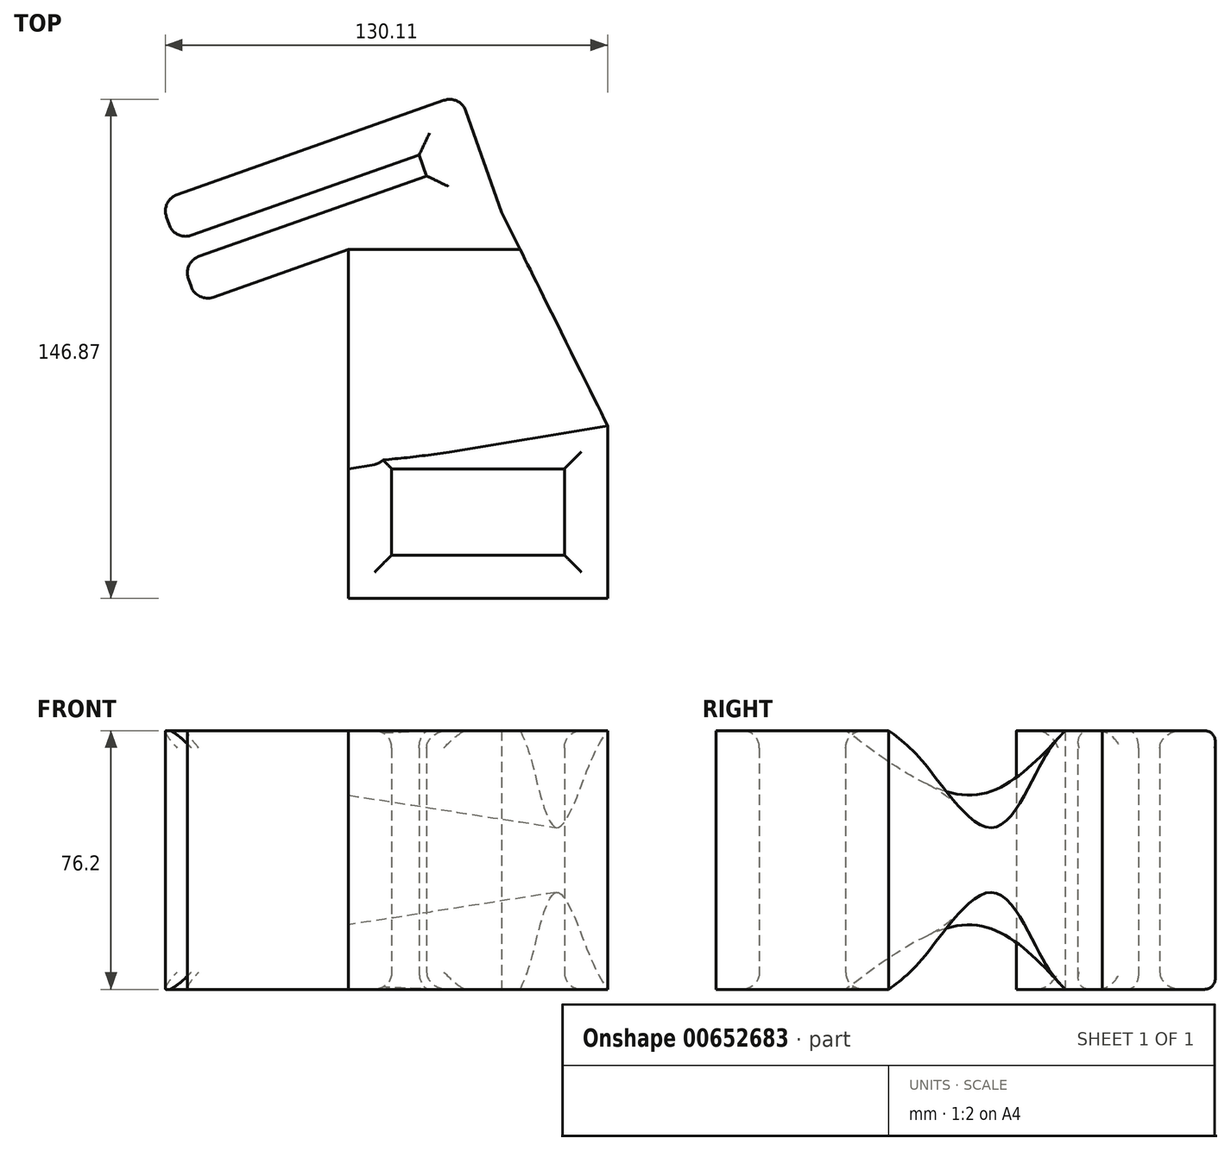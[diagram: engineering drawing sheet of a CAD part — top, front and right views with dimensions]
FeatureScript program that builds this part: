
annotation { "Feature Type Name" : "Feature", "Feature Type Description" : "" }
export const myFeature = defineFeature(function(context is Context, id is Id, definition is map)
    precondition{}
    {
        {
            var Q0;
            Q0=qCreatedBy(makeId("Top.planeOp"),FACE);
            var sketch = newSketch(context, id + "F0", { "sketchPlane" : qUnion([Q0])});
            skLineSegment(sketch, "E0.bottom", {"start": v(-25.4, -12.7) * mm, "end": v(25.4, -12.7) * mm});
            skLineSegment(sketch, "E0.top", {"start": v(-25.4, 12.7) * mm, "end": v(25.4, 12.7) * mm});
            skLineSegment(sketch, "E0.left", {"start": v(-25.4, -12.7) * mm, "end": v(-25.4, 12.7) * mm});
            skLineSegment(sketch, "E0.right", {"start": v(25.4, -12.7) * mm, "end": v(25.4, 12.7) * mm});
            skPoint(sketch, "E0.middle", {"position": v(0, 0) * mm});
            skLineSegment(sketch, "E1.bottom", {"start": v(-38.1, -25.4) * mm, "end": v(38.1, -25.4) * mm});
            skLineSegment(sketch, "E1.top", {"start": v(-38.1, 25.4) * mm, "end": v(38.1, 25.4) * mm});
            skLineSegment(sketch, "E1.left", {"start": v(-38.1, -25.4) * mm, "end": v(-38.1, 25.4) * mm});
            skLineSegment(sketch, "E1.right", {"start": v(38.1, -25.4) * mm, "end": v(38.1, 25.4) * mm});
            skLineSegment(sketch, "E2", {"start": v(0, 0) * mm, "end": v(-304.8, 0) * mm, "construction": true});
            skLineSegment(sketch, "E3", {"start": v(-304.8, 0) * mm, "end": v(-17.43, 101.6) * mm, "construction": true});
            skLineSegment(sketch, "E4", {"start": v(-89.18, 79.74) * mm, "end": v(-17.34, 105.14) * mm});
            skLineSegment(sketch, "E5", {"start": v(-17.34, 105.14) * mm, "end": v(-15.13, 98.91) * mm});
            skLineSegment(sketch, "E6", {"start": v(-15.13, 98.91) * mm, "end": v(-86.98, 73.51) * mm});
            skLineSegment(sketch, "E7", {"start": v(-89.18, 79.74) * mm, "end": v(-93.41, 91.71) * mm});
            skLineSegment(sketch, "E8", {"start": v(-93.41, 91.71) * mm, "end": v(-5.26, 122.87) * mm});
            skLineSegment(sketch, "E9", {"start": v(-5.26, 122.87) * mm, "end": v(6.98, 88.25) * mm});
            skLineSegment(sketch, "E10", {"start": v(6.98, 88.25) * mm, "end": v(38.1, 25.4) * mm});
            skLineSegment(sketch, "E11", {"start": v(-86.98, 73.51) * mm, "end": v(-82.74, 61.54) * mm});
            skLineSegment(sketch, "E12", {"start": v(-82.74, 61.54) * mm, "end": v(-38.1, 77.32) * mm});
            skLineSegment(sketch, "E13", {"start": v(-38.1, 77.32) * mm, "end": v(-38.1, 25.4) * mm});
            skSolve(sketch);
        }
        {
            var Q0;
            Q0=makeQuery(id+"F0.imprint","IMPRINT",FACE,{"disambiguationData":[TD([[makeQuery(id+"F0.imprint","IMPRINT",EDGE,{"derivedFrom":sQuery(id+"F0.wireOp",EDGE,"E1.top")}),1.0]])]});
            var Q1;
            Q1=makeQuery(id+"F0.imprint","IMPRINT",FACE,{"disambiguationData":[TD([[makeQuery(id+"F0.imprint","IMPRINT",EDGE,{"derivedFrom":sQuery(id+"F0.wireOp",EDGE,"E0.bottom")}),-1.0]])]});
            extrude(context, id + "F1", {"entities" : qUnion([Q0, Q1]), "depth" : 76.2 * mm, "offsetDistance" : 25.4 * mm});
        }
        {
            var Q0;
            Q0=makeQuery(id+"F1.opExtrude","SWEPT_FACE",FACE,{"disambiguationData":[OSD([sQuery(id+"F0.wireOp",EDGE,"E1.left"),sQuery(id+"F0.wireOp",EDGE,"E13")])]});
            var sketch = newSketch(context, id + "F2", { "sketchPlane" : qUnion([Q0])});
            skLineSegment(sketch, "E14.0", {"start": v(-12.7, 76.2) * mm, "end": v(-12.7, 0) * mm, "construction": true});
            skLineSegment(sketch, "E15.0", {"start": v(-77.32, 76.2) * mm, "end": v(-77.32, 0) * mm, "construction": true});
            skLineSegment(sketch, "E16", {"start": v(25.4, 38.1) * mm, "end": v(-77.32, 38.1) * mm});
            skFitSpline(sketch, "E17", {"points": [v(-77.32, 76.2) * mm, v(-50.46, 57.23) * mm, v(-12.7, 76.2) * mm], "startDerivative": vector(54.08, -58.32) * mm, "endDerivative": vector(74.73, 55.94) * mm});
            skFitSpline(sketch, "E18.MirrorCS", {"points": [v(-77.32, 0) * mm, v(-50.46, 18.97) * mm, v(-12.7, 0) * mm], "startDerivative": vector(54.08, 58.32) * mm, "endDerivative": vector(74.73, -55.94) * mm});
            skSolve(sketch);
        }
        {
            var Q0;
            Q0=makeQuery(id+"F1.opExtrude","SWEPT_FACE",FACE,{"disambiguationData":[OSD([sQuery(id+"F0.wireOp",EDGE,"E10")])]});
            var sketch = newSketch(context, id + "F3", { "sketchPlane" : qUnion([Q0])});
            skFitSpline(sketch, "E19.0", {"points": [v(63.76, 76.2) * mm, v(56.2, 67.09) * mm, v(40.04, 47.65) * mm, v(17.72, 66.3) * mm, v(5.86, 76.2) * mm]});
            skFitSpline(sketch, "E20.0", {"points": [v(63.76, 0) * mm, v(56.2, 9.11) * mm, v(40.04, 28.55) * mm, v(17.72, 9.9) * mm, v(5.86, 0) * mm]});
            skSolve(sketch);
        }
        {
            var Q1;
            {var subQ0=sQuery(id+"F2.wireOp",EDGE,"E17");Q1=makeQuery(id+"F2.imprint","IMPRINT",FACE,{"disambiguationData":[TD([[makeQuery(id+"F2.imprint","IMPRINT",EDGE,{"derivedFrom":subQ0}),1.0]])]});}
            var Q2;
            {var subQ0=sQuery(id+"F3.wireOp",EDGE,"E19.0");Q2=makeQuery(id+"F3.imprint","IMPRINT",FACE,{"disambiguationData":[TD([[makeQuery(id+"F3.imprint","IMPRINT",EDGE,{"derivedFrom":subQ0}),-1.0]])]});}
            loft(context, id + "F4", {"operationType" : NewBodyOperationType.REMOVE, "sheetProfilesArray" : [{ "sheetProfileEntities" : qUnion([Q1]) }, { "sheetProfileEntities" : qUnion([Q2]) }]});
        }
        {
            var Q1;
            {var subQ0=sQuery(id+"F2.wireOp",EDGE,"E18.MirrorCS");Q1=makeQuery(id+"F2.imprint","IMPRINT",FACE,{"disambiguationData":[TD([[makeQuery(id+"F2.imprint","IMPRINT",EDGE,{"derivedFrom":subQ0}),-1.0]])]});}
            var Q2;
            {var subQ0=sQuery(id+"F3.wireOp",EDGE,"E20.0");Q2=makeQuery(id+"F3.imprint","IMPRINT",FACE,{"disambiguationData":[TD([[makeQuery(id+"F3.imprint","IMPRINT",EDGE,{"derivedFrom":subQ0}),1.0]])]});}
            loft(context, id + "F5", {"operationType" : NewBodyOperationType.REMOVE, "sheetProfilesArray" : [{ "sheetProfileEntities" : qUnion([Q1]) }, { "sheetProfileEntities" : qUnion([Q2]) }]});
        }
        {
            var Q0;
            Q0=makeQuery(id+"F1.opExtrude","CAP_EDGE",EDGE,{"disambiguationData":[OSD([sQuery(id+"F0.wireOp",EDGE,"E4")])],"isStart":false});
            var Q1;
            Q1=makeQuery(id+"F1.opExtrude","CAP_EDGE",EDGE,{"disambiguationData":[OSD([sQuery(id+"F0.wireOp",EDGE,"E5")])],"isStart":false});
            var Q2;
            Q2=makeQuery(id+"F1.opExtrude","CAP_EDGE",EDGE,{"disambiguationData":[OSD([sQuery(id+"F0.wireOp",EDGE,"E6")])],"isStart":false});
            var Q3;
            Q3=makeQuery(id+"F1.opExtrude","SWEPT_EDGE",EDGE,{"disambiguationData":[OSD([sQuery(id+"F0.wireOp",EDGE,"E4"),sQuery(id+"F0.wireOp",EDGE,"E7")])]});
            var Q4;
            Q4=makeQuery(id+"F1.opExtrude","SWEPT_EDGE",EDGE,{"disambiguationData":[OSD([sQuery(id+"F0.wireOp",EDGE,"E6"),sQuery(id+"F0.wireOp",EDGE,"E11")])]});
            var Q5;
            Q5=makeQuery(id+"F1.opExtrude","CAP_EDGE",EDGE,{"disambiguationData":[OSD([sQuery(id+"F0.wireOp",EDGE,"E4")])],"isStart":true});
            var Q6;
            Q6=makeQuery(id+"F1.opExtrude","CAP_EDGE",EDGE,{"disambiguationData":[OSD([sQuery(id+"F0.wireOp",EDGE,"E6")])],"isStart":true});
            var Q7;
            Q7=makeQuery(id+"F1.opExtrude","SWEPT_EDGE",EDGE,{"disambiguationData":[OSD([sQuery(id+"F0.wireOp",EDGE,"E7"),sQuery(id+"F0.wireOp",EDGE,"E8")])]});
            var Q8;
            Q8=makeQuery(id+"F1.opExtrude","CAP_EDGE",EDGE,{"disambiguationData":[OSD([sQuery(id+"F0.wireOp",EDGE,"E8")])],"isStart":false});
            var Q9;
            Q9=makeQuery(id+"F1.opExtrude","CAP_EDGE",EDGE,{"disambiguationData":[OSD([sQuery(id+"F0.wireOp",EDGE,"E8")])],"isStart":true});
            var Q10;
            Q10=makeQuery(id+"F1.opExtrude","SWEPT_EDGE",EDGE,{"disambiguationData":[OSD([sQuery(id+"F0.wireOp",EDGE,"E8"),sQuery(id+"F0.wireOp",EDGE,"E9")])]});
            var Q11;
            Q11=makeQuery(id+"F1.opExtrude","CAP_EDGE",EDGE,{"disambiguationData":[OSD([sQuery(id+"F0.wireOp",EDGE,"E5")])],"isStart":true});
            var Q12;
            Q12=makeQuery(id+"F1.opExtrude","CAP_EDGE",EDGE,{"disambiguationData":[OSD([sQuery(id+"F0.wireOp",EDGE,"E0.top")])],"isStart":false});
            var Q13;
            Q13=makeQuery(id+"F1.opExtrude","CAP_EDGE",EDGE,{"disambiguationData":[OSD([sQuery(id+"F0.wireOp",EDGE,"E0.left")])],"isStart":false});
            var Q14;
            Q14=makeQuery(id+"F1.opExtrude","CAP_EDGE",EDGE,{"disambiguationData":[OSD([sQuery(id+"F0.wireOp",EDGE,"E0.bottom")])],"isStart":false});
            var Q15;
            Q15=makeQuery(id+"F1.opExtrude","CAP_EDGE",EDGE,{"disambiguationData":[OSD([sQuery(id+"F0.wireOp",EDGE,"E0.right")])],"isStart":false});
            var Q16;
            Q16=makeQuery(id+"F1.opExtrude","CAP_EDGE",EDGE,{"disambiguationData":[OSD([sQuery(id+"F0.wireOp",EDGE,"E0.left")])],"isStart":true});
            var Q17;
            Q17=makeQuery(id+"F1.opExtrude","CAP_EDGE",EDGE,{"disambiguationData":[OSD([sQuery(id+"F0.wireOp",EDGE,"E0.top")])],"isStart":true});
            var Q18;
            Q18=makeQuery(id+"F1.opExtrude","CAP_EDGE",EDGE,{"disambiguationData":[OSD([sQuery(id+"F0.wireOp",EDGE,"E0.right")])],"isStart":true});
            var Q19;
            Q19=makeQuery(id+"F1.opExtrude","CAP_EDGE",EDGE,{"disambiguationData":[OSD([sQuery(id+"F0.wireOp",EDGE,"E0.bottom")])],"isStart":true});
            var Q20;
            Q20=makeQuery(id+"F4.boolean.opBoolean","COPY",EDGE,{"derivedFrom":makeQuery(id+"F4.opLoft","SWEPT_EDGE",EDGE,{"disambiguationData":[OSD([sQuery(id+"F0.wireOp",EDGE,"E1.left"),sQuery(id+"F0.wireOp",EDGE,"E10"),sQuery(id+"F0.wireOp",EDGE,"E12"),sQuery(id+"F0.wireOp",EDGE,"E13"),sQuery(id+"F2.wireOp",EDGE,"E17"),sQuery(id+"F3.wireOp",EDGE,"E19.0")])]})});
            var Q21;
            Q21=makeQuery(id+"F5.boolean.opBoolean","COPY",EDGE,{"derivedFrom":makeQuery(id+"F5.opLoft","SWEPT_EDGE",EDGE,{"disambiguationData":[OSD([sQuery(id+"F0.wireOp",EDGE,"E1.left"),sQuery(id+"F0.wireOp",EDGE,"E10"),sQuery(id+"F0.wireOp",EDGE,"E12"),sQuery(id+"F0.wireOp",EDGE,"E13"),sQuery(id+"F2.wireOp",EDGE,"E18.MirrorCS"),sQuery(id+"F3.wireOp",EDGE,"E20.0")])]})});
            var Q22;
            Q22=makeQuery(id+"F1.opExtrude","SWEPT_EDGE",EDGE,{"disambiguationData":[OSD([sQuery(id+"F0.wireOp",EDGE,"E11"),sQuery(id+"F0.wireOp",EDGE,"E12")])]});
            fillet(context, id + "F6", {"entities" : qUnion([Q0, Q1, Q2, Q3, Q4, Q5, Q6, Q7, Q8, Q9, Q10, Q11, Q12, Q13, Q14, Q15, Q16, Q17, Q18, Q19, Q20, Q21, Q22]), "radius" : 5.08 * mm, "tangentPropagation" : true, "allowEdgeOverflow" : false});
        }
    });
